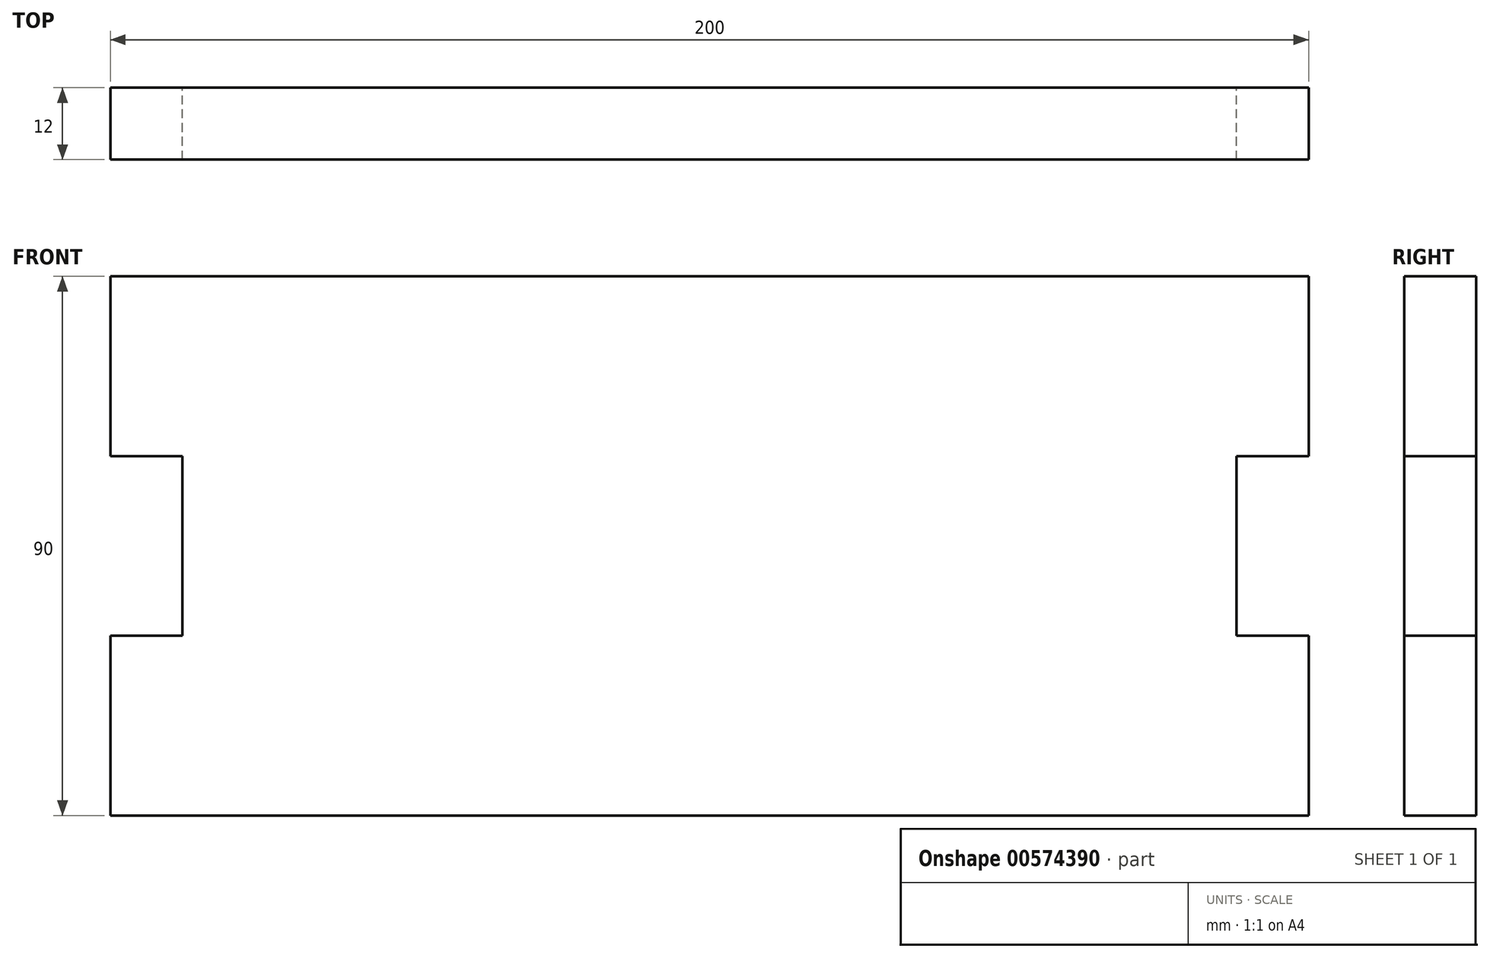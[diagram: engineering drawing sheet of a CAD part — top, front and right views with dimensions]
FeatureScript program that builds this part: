
annotation { "Feature Type Name" : "Feature", "Feature Type Description" : "" }
export const myFeature = defineFeature(function(context is Context, id is Id, definition is map)
    precondition{}
    {
        {
            var Q0;
            Q0=qCreatedBy(makeId("Front.planeOp"),FACE);
            var sketch = newSketch(context, id + "F0", { "sketchPlane" : qUnion([Q0])});
            skLineSegment(sketch, "E0", {"start": v(0, 0) * mm, "end": v(0, 30) * mm});
            skLineSegment(sketch, "E1", {"start": v(0, 30) * mm, "end": v(12, 30) * mm});
            skLineSegment(sketch, "E2", {"start": v(12, 30) * mm, "end": v(12, 60) * mm});
            skLineSegment(sketch, "E3", {"start": v(12, 60) * mm, "end": v(0, 60) * mm});
            skLineSegment(sketch, "E4", {"start": v(0, 60) * mm, "end": v(0, 90) * mm});
            skLineSegment(sketch, "E5", {"start": v(0, 90) * mm, "end": v(100, 90) * mm});
            skLineSegment(sketch, "E6", {"start": v(100, 90) * mm, "end": v(100, 0) * mm, "construction": true});
            skLineSegment(sketch, "E7", {"start": v(100, 0) * mm, "end": v(0, 0) * mm});
            skLineSegment(sketch, "E8.MirrorCS", {"start": v(200, 30) * mm, "end": v(188, 30) * mm});
            skLineSegment(sketch, "E9.MirrorCS", {"start": v(100, 0) * mm, "end": v(200, 0) * mm});
            skLineSegment(sketch, "E10.MirrorCS", {"start": v(200, 60) * mm, "end": v(200, 90) * mm});
            skLineSegment(sketch, "E11.MirrorCS", {"start": v(200, 0) * mm, "end": v(200, 30) * mm});
            skLineSegment(sketch, "E12.MirrorCS", {"start": v(188, 60) * mm, "end": v(200, 60) * mm});
            skLineSegment(sketch, "E13.MirrorCS", {"start": v(188, 30) * mm, "end": v(188, 60) * mm});
            skLineSegment(sketch, "E14.MirrorCS", {"start": v(200, 90) * mm, "end": v(100, 90) * mm});
            skSolve(sketch);
        }
        {
            var Q0;
            Q0=makeQuery(id+"F0.imprint","IMPRINT",FACE,{"disambiguationData":[TD([[makeQuery(id+"F0.imprint","IMPRINT",EDGE,{"derivedFrom":sQuery(id+"F0.wireOp",EDGE,"E0")}),-1.0]])]});
            extrude(context, id + "F1", {"entities" : qUnion([Q0]), "depth" : 12 * mm, "offsetDistance" : 25 * mm});
        }
    });
